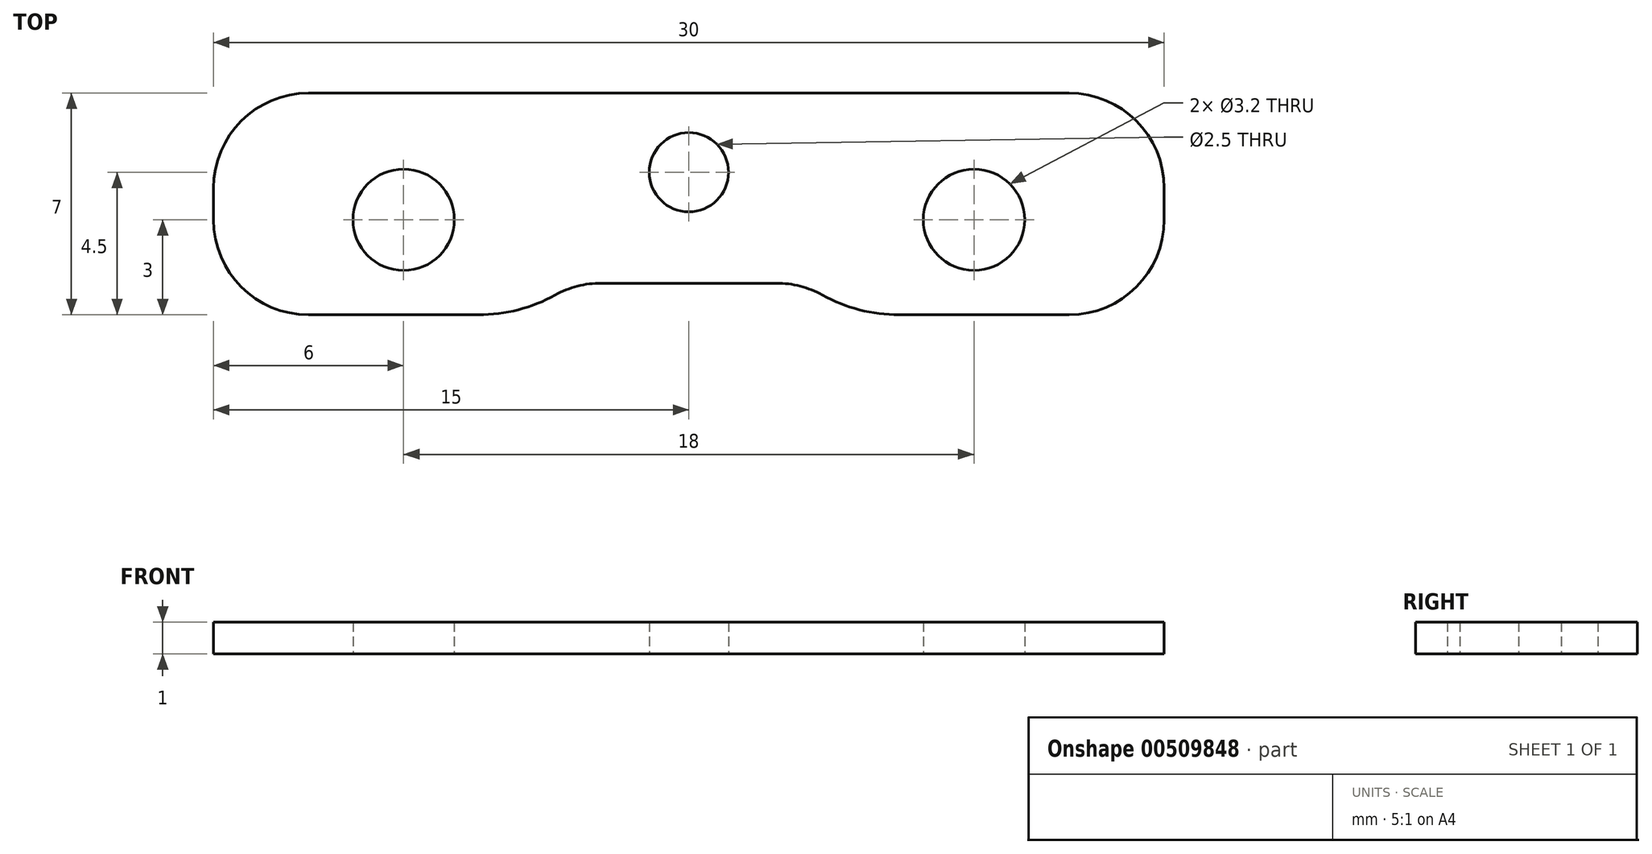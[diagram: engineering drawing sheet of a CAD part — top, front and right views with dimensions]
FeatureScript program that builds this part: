
annotation { "Feature Type Name" : "Feature", "Feature Type Description" : "" }
export const myFeature = defineFeature(function(context is Context, id is Id, definition is map)
    precondition{}
    {
        {
            var Q0;
            Q0=qCreatedBy(makeId("Top.planeOp"),FACE);
            var sketch = newSketch(context, id + "F0", { "sketchPlane" : qUnion([Q0])});
            skLineSegment(sketch, "E0.bottom", {"start": v(15, 3.5) * mm, "end": v(5, 3.5) * mm});
            skLineSegment(sketch, "E0.top", {"start": v(15, -3.5) * mm, "end": v(5, -3.5) * mm});
            skLineSegment(sketch, "E0.left", {"start": v(15, 3.5) * mm, "end": v(15, -3.5) * mm});
            skLineSegment(sketch, "E0.right", {"start": v(-15, 3.5) * mm, "end": v(-15, -3.5) * mm});
            skPoint(sketch, "E0.middle", {"position": v(0, 0) * mm});
            skCircle(sketch, "E1", {"center": v(-9, -0.5) * mm, "radius": 1.6 * mm});
            skCircle(sketch, "E2", {"center": v(9, -0.5) * mm, "radius": 1.6 * mm});
            skLineSegment(sketch, "E3", {"start": v(-5, -3.5) * mm, "end": v(-5, -2.5) * mm});
            skLineSegment(sketch, "E4", {"start": v(-5, -2.5) * mm, "end": v(5, -2.5) * mm});
            skLineSegment(sketch, "E5", {"start": v(5, -2.5) * mm, "end": v(5, -3.5) * mm});
            skLineSegment(sketch, "E6", {"start": v(-5, 3.5) * mm, "end": v(-5, 3.5) * mm});
            skLineSegment(sketch, "E7", {"start": v(-5, 3.5) * mm, "end": v(5, 3.5) * mm});
            skLineSegment(sketch, "E8", {"start": v(5, 3.5) * mm, "end": v(5, 3.5) * mm});
            skLineSegment(sketch, "E9.trimOffspring", {"start": v(-5, 3.5) * mm, "end": v(-15, 3.5) * mm});
            skLineSegment(sketch, "E10.trimOffspring", {"start": v(-5, -3.5) * mm, "end": v(-15, -3.5) * mm});
            skCircle(sketch, "E11", {"center": v(0, 1) * mm, "radius": 1.25 * mm});
            skSolve(sketch);
        }
        {
            var Q0;
            Q0 = qSketchRegion(id + "F0", true);
            extrude(context, id + "F1", {"entities" : qUnion([Q0]), "depth" : 1 * mm});
        }
        {
            var Q0;
            Q0=makeQuery(id+"F1.opExtrude","SWEPT_EDGE",EDGE,{"disambiguationData":[OSD([sQuery(id+"F0.wireOp",EDGE,"E3"),sQuery(id+"F0.wireOp",EDGE,"E4")])]});
            var Q1;
            Q1=makeQuery(id+"F1.opExtrude","SWEPT_EDGE",EDGE,{"disambiguationData":[OSD([sQuery(id+"F0.wireOp",EDGE,"E4"),sQuery(id+"F0.wireOp",EDGE,"E5")])]});
            var Q2;
            Q2=makeQuery(id+"F1.opExtrude","SWEPT_EDGE",EDGE,{"disambiguationData":[OSD([sQuery(id+"F0.wireOp",EDGE,"E0.right"),sQuery(id+"F0.wireOp",EDGE,"E10.trimOffspring")])]});
            var Q3;
            Q3=makeQuery(id+"F1.opExtrude","SWEPT_EDGE",EDGE,{"disambiguationData":[OSD([sQuery(id+"F0.wireOp",EDGE,"E0.right"),sQuery(id+"F0.wireOp",EDGE,"E9.trimOffspring")])]});
            var Q4;
            Q4=makeQuery(id+"F1.opExtrude","SWEPT_EDGE",EDGE,{"disambiguationData":[OSD([sQuery(id+"F0.wireOp",EDGE,"E0.top"),sQuery(id+"F0.wireOp",EDGE,"E0.left")])]});
            var Q5;
            Q5=makeQuery(id+"F1.opExtrude","SWEPT_EDGE",EDGE,{"disambiguationData":[OSD([sQuery(id+"F0.wireOp",EDGE,"E0.bottom"),sQuery(id+"F0.wireOp",EDGE,"E0.left")])]});
            fillet(context, id + "F2", {"entities" : qUnion([Q0, Q1, Q2, Q3, Q4, Q5]), "radius" : 3 * mm, "tangentPropagation" : true, "allowEdgeOverflow" : false});
        }
        {
            var Q0;
            Q0=makeQuery(id+"F2.opFillet","BLEND_EDGE",EDGE,{"blendedFrom":[makeQuery(id+"F1.opExtrude","SWEPT_EDGE",EDGE,{"disambiguationData":[OSD([sQuery(id+"F0.wireOp",EDGE,"E3"),sQuery(id+"F0.wireOp",EDGE,"E4")])]}),makeQuery(id+"F1.opExtrude","SWEPT_FACE",FACE,{"disambiguationData":[OSD([sQuery(id+"F0.wireOp",EDGE,"E10.trimOffspring")])]})],"blendedInto":[makeQuery(id+"F1.opExtrude","SWEPT_FACE",FACE,{"disambiguationData":[OSD([sQuery(id+"F0.wireOp",EDGE,"E10.trimOffspring")])]})]});
            var Q1;
            Q1=makeQuery(id+"F2.opFillet","BLEND_EDGE",EDGE,{"blendedFrom":[makeQuery(id+"F1.opExtrude","SWEPT_EDGE",EDGE,{"disambiguationData":[OSD([sQuery(id+"F0.wireOp",EDGE,"E4"),sQuery(id+"F0.wireOp",EDGE,"E5")])]}),makeQuery(id+"F1.opExtrude","SWEPT_FACE",FACE,{"disambiguationData":[OSD([sQuery(id+"F0.wireOp",EDGE,"E0.top")])]})],"blendedInto":[makeQuery(id+"F1.opExtrude","SWEPT_FACE",FACE,{"disambiguationData":[OSD([sQuery(id+"F0.wireOp",EDGE,"E0.top")])]})]});
            fillet(context, id + "F3", {"entities" : qUnion([Q0, Q1]), "radius" : 5 * mm, "tangentPropagation" : true, "allowEdgeOverflow" : false});
        }
    });
